# Revit family: Sanext_Трубка T-образная d15 для подключения радиатора
name_source: partatom
category: Соединительные детали трубопроводов
revit_build: Autodesk Revit 2017 (Build: 20160225_1515(x64)
units: mm (PartAtom-declared; Revit-internal decimal feet)

## family parameters
Всегда вертикально = Да
На основе рабочей плоскости = Нет
Общий = Нет
При загрузке вырезать с полостями = Нет
Размер круглого соединителя = Использовать радиус
Тип детали = Тройник

## types (7) — shared parameters
ADSK_Единица измерения = шт
ADSK_Завод-изготовитель = Sanext
ID20 = Фитинг подключения L и T-обазных трубок d15 : Фитинг подключения L и T-образных трубок d15xR1/2 c резиновым уплотнителем
ID25 = Фитинг подключения L и T-обазных трубок d15 : Фитинг подключения L и T-образных трубок d15xG3/4 евроконус
R_10 = 10 мм
URL = http://sanext.ru
Изготовитель = Sanext
Материал фитинга = DZR латунь
Разработчик = ООО ПРОРУБИМ
Разработчик (телефон) = +7(495)649-85-43
Разработчик модели (URL) = http://prorubim.com
zero-valued in all types: ADSK_Масса

## per-type parameters (varying)
| type | ADSK_Код изделия | ADSK_Наименование | DN | DN2 |
| Трубка Т-образная d15 для подключения радиатора 25x15х25 | 4810 | Трубка Т-образная d15 для подключения радиатора 16x15x16 | 16 мм | 16 мм |
| Трубка Т-образная d15 для подключения радиатора 25x15x20 | 4832 | Трубка Т-образная d15 для подключения радиатора 25x15x20 | 25 мм | 20 мм |
| Трубка Т-образная d15 для подключения радиатора 20x15x25 | 4823 | Трубка Т-образная d15 для подключения радиатора 20x15x25 | 20 мм | 25 мм |
| Трубка Т-образная d15 для подключения радиатора 20x15x20 | 4820 | Трубка Т-образная d15 для подключения радиатора 20x15x20 | 20 мм | 20 мм |
| Трубка Т-образная d15 для подключения радиатора 20x15x16 | 4821 | Трубка Т-образная d15 для подключения радиатора 20x15x16 | 20 мм | 16 мм |
| Трубка Т-образная d15 для подключения радиатора 16x15x20 | 4812 | Трубка Т-образная d15 для подключения радиатора 16x15x20 | 16 мм | 20 мм |
| Трубка Т-образная d15 для подключения радиатора 16x15x16 | 4810 | Трубка Т-образная d15 для подключения радиатора 16x15x16 | 16 мм | 16 мм |
